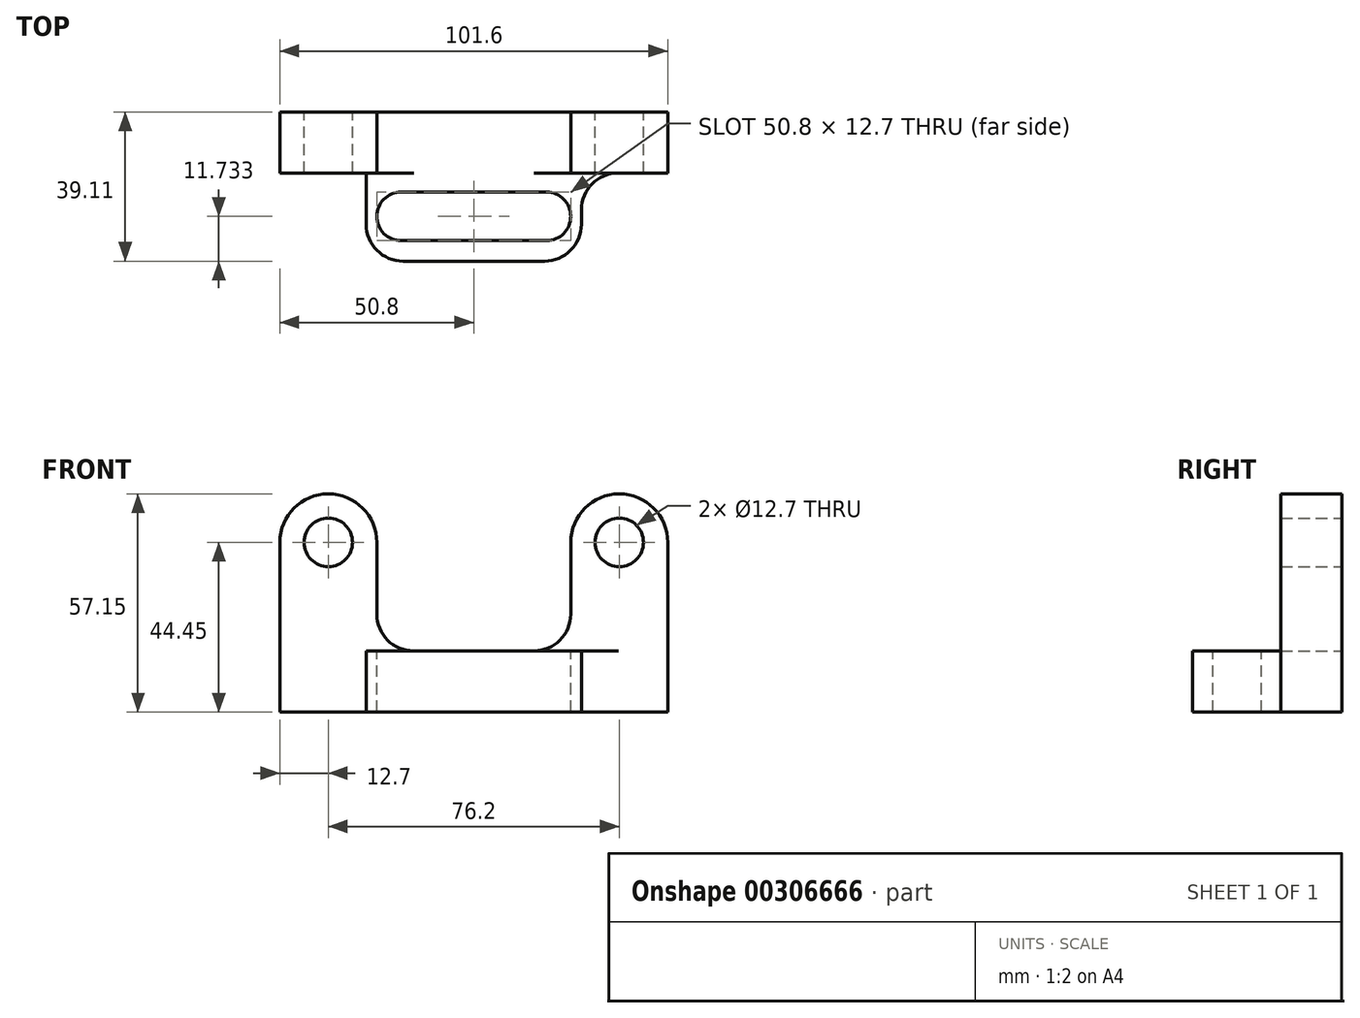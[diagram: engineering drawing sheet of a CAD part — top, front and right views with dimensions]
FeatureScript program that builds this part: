
annotation { "Feature Type Name" : "Feature", "Feature Type Description" : "" }
export const myFeature = defineFeature(function(context is Context, id is Id, definition is map)
    precondition{}
    {
        {
            var Q0;
            Q0=qCreatedBy(makeId("Front.planeOp"),FACE);
            var sketch = newSketch(context, id + "F0", { "sketchPlane" : qUnion([Q0])});
            skLineSegment(sketch, "E0", {"start": v(0, 0) * mm, "end": v(-50.8, 0) * mm});
            skLineSegment(sketch, "E1", {"start": v(-50.8, 0) * mm, "end": v(-50.8, 44.45) * mm});
            skLineSegment(sketch, "E2", {"start": v(-25.4, 44.45) * mm, "end": v(-25.4, 16) * mm});
            skLineSegment(sketch, "E3", {"start": v(-25.4, 16) * mm, "end": v(0, 16) * mm});
            skLineSegment(sketch, "E4", {"start": v(0, 0) * mm, "end": v(0, 78.5) * mm, "construction": true});
            skLineSegment(sketch, "E5.MirrorCS", {"start": v(25.4, 16) * mm, "end": v(0, 16) * mm});
            skLineSegment(sketch, "E6.MirrorCS", {"start": v(25.4, 44.45) * mm, "end": v(25.4, 16) * mm});
            skLineSegment(sketch, "E7.MirrorCS", {"start": v(50.8, 0) * mm, "end": v(50.8, 44.45) * mm});
            skLineSegment(sketch, "E8.MirrorCS", {"start": v(0, 0) * mm, "end": v(50.8, 0) * mm});
            skCircle(sketch, "E9", {"center": v(38.1, 44.45) * mm, "radius": 6.35 * mm});
            skCircle(sketch, "E10.MirrorC", {"center": v(-38.1, 44.45) * mm, "radius": 6.35 * mm});
            skLineSegment(sketch, "E11", {"start": v(38.1, 44.45) * mm, "end": v(38.1, 67.53) * mm, "construction": true});
            skLineSegment(sketch, "E12", {"start": v(-38.1, 44.45) * mm, "end": v(-38.1, 65.76) * mm, "construction": true});
            skArc(sketch, "E13", {"start": v(38.1, 57.15) * mm, "mid": v(29.12, 53.43) * mm, "end": v(25.4, 44.45) * mm});
            skArc(sketch, "E14", {"start": v(38.1, 57.15) * mm, "mid": v(47.08, 53.43) * mm, "end": v(50.8, 44.45) * mm});
            skArc(sketch, "E15.MirrorCS", {"start": v(-38.1, 57.15) * mm, "mid": v(-29.12, 53.43) * mm, "end": v(-25.4, 44.45) * mm});
            skArc(sketch, "E16.MirrorCS", {"start": v(-38.1, 57.15) * mm, "mid": v(-47.08, 53.43) * mm, "end": v(-50.8, 44.45) * mm});
            skPoint(sketch, "E17.orphan", {"position": v(50.8, 57.15) * mm});
            skPoint(sketch, "E18.MirrorCS.end.orphan", {"position": v(25.4, 57.15) * mm});
            skPoint(sketch, "E19.orphan", {"position": v(-25.4, 57.15) * mm});
            skPoint(sketch, "E20.orphan", {"position": v(-50.8, 57.15) * mm});
            skSolve(sketch);
        }
        {
            var Q0;
            {var subQ5=sQuery(id+"F0.wireOp",EDGE,"E0");Q0=makeQuery(id+"F0.imprint","IMPRINT",FACE,{"disambiguationData":[TD([[makeQuery(id+"F0.imprint","IMPRINT",EDGE,{"derivedFrom":subQ5}),-1.0]])]});}
            extrude(context, id + "F1", {"entities" : qUnion([Q0]), "depth" : 16 * mm});
        }
        {
            var Q0;
            Q0=makeQuery(id+"F0.imprint","IMPRINT",FACE,{"disambiguationData":[TD([[makeQuery(id+"F0.imprint","IMPRINT",EDGE,{"derivedFrom":sQuery(id+"F0.wireOp",EDGE,"E0")}),-1.0]])]});
            extrude(context, id + "F2", {"entities" : qUnion([Q0]), "operationType" : NewBodyOperationType.ADD, "depth" : 16 * mm});
        }
        {
            var Q0;
            Q0=makeQuery(id+"F1.opExtrude","SWEPT_EDGE",EDGE,{"disambiguationData":[OSD([sQuery(id+"F0.wireOp",EDGE,"E2"),sQuery(id+"F0.wireOp",EDGE,"E3")])]});
            var Q1;
            Q1=makeQuery(id+"F1.opExtrude","SWEPT_EDGE",EDGE,{"disambiguationData":[OSD([sQuery(id+"F0.wireOp",EDGE,"E5.MirrorCS"),sQuery(id+"F0.wireOp",EDGE,"E6.MirrorCS")])]});
            fillet(context, id + "F3", {"entities" : qUnion([Q0, Q1]), "radius" : 9.65 * mm, "tangentPropagation" : true, "allowEdgeOverflow" : false});
        }
        {
            var Q0;
            Q0=qCreatedBy(makeId("Top.planeOp"),FACE);
            var sketch = newSketch(context, id + "F4", { "sketchPlane" : qUnion([Q0])});
            skLineSegment(sketch, "E21", {"start": v(28.17, -16) * mm, "end": v(28.17, -39.11) * mm});
            skLineSegment(sketch, "E22.MirrorCS", {"start": v(-28.17, -16) * mm, "end": v(-28.17, -39.11) * mm});
            skLineSegment(sketch, "E23", {"start": v(-28.17, -39.11) * mm, "end": v(28.17, -39.11) * mm});
            skLineSegment(sketch, "E24", {"start": v(-28.17, -16) * mm, "end": v(28.17, -16) * mm});
            skSolve(sketch);
        }
        {
            var Q0;
            Q0=makeQuery(id+"F4.imprint","IMPRINT",FACE,{"disambiguationData":[TD([[makeQuery(id+"F4.imprint","IMPRINT",EDGE,{"derivedFrom":sQuery(id+"F4.wireOp",EDGE,"E21")}),-1.0]])]});
            extrude(context, id + "F5", {"entities" : qUnion([Q0]), "operationType" : NewBodyOperationType.ADD, "depth" : 16 * mm});
        }
        {
            var Q0;
            Q0=makeQuery(id+"F5.boolean.opBoolean","MERGE",FACE,{"derivedFrom":[makeQuery(id+"F1.opExtrude","SWEPT_FACE",FACE,{"disambiguationData":[OSD([sQuery(id+"F0.wireOp",EDGE,"E3"),sQuery(id+"F0.wireOp",EDGE,"E5.MirrorCS")])]}),makeQuery(id+"F5.opExtrude","CAP_FACE",FACE,{"disambiguationData":[OSD([sQuery(id+"F4.wireOp",EDGE,"E21"),sQuery(id+"F4.wireOp",EDGE,"KRn6xeVq-3zaL-ZNE9-6kKy-dGFoVnLs3Zqx"),sQuery(id+"F4.wireOp",EDGE,"ae659aa5-0c71-4b39-b7c4-d228686435f50.MirrorCS"),sQuery(id+"F4.wireOp",EDGE,"E22.MirrorCS"),sQuery(id+"F4.wireOp",EDGE,"PJdEW5La-l0Tz-svzj-1M6O-rA534kSb0CCf"),sQuery(id+"F4.wireOp",EDGE,"3d896502-7fe0-40ef-a271-82883b495ef90.MirrorCS")])],"isStart":false})]});
            var sketch = newSketch(context, id + "F6", { "sketchPlane" : qUnion([Q0])});
            skLineSegment(sketch, "E25", {"start": v(0, -21.03) * mm, "end": v(19.05, -21.03) * mm});
            skLineSegment(sketch, "E26", {"start": v(0, -33.73) * mm, "end": v(19.05, -33.73) * mm});
            skArc(sketch, "E27", {"start": v(19.05, -33.73) * mm, "mid": v(25.4, -27.38) * mm, "end": v(19.05, -21.03) * mm});
            skLineSegment(sketch, "E28.MirrorCS", {"start": v(0, -21.03) * mm, "end": v(-19.05, -21.03) * mm});
            skLineSegment(sketch, "E29.MirrorCS", {"start": v(0, -33.73) * mm, "end": v(-19.05, -33.73) * mm});
            skArc(sketch, "E30.MirrorCS", {"start": v(-19.05, -33.73) * mm, "mid": v(-25.4, -27.38) * mm, "end": v(-19.05, -21.03) * mm});
            skSolve(sketch);
        }
        {
            var Q0;
            Q0=makeQuery(id+"F5.opExtrude","SWEPT_EDGE",EDGE,{"disambiguationData":[OSD([sQuery(id+"F4.wireOp",EDGE,"E21"),sQuery(id+"F4.wireOp",EDGE,"E23")])]});
            var Q1;
            Q1=makeQuery(id+"F5.opExtrude","SWEPT_EDGE",EDGE,{"disambiguationData":[OSD([sQuery(id+"F4.wireOp",EDGE,"E22.MirrorCS"),sQuery(id+"F4.wireOp",EDGE,"E23")])]});
            var Q2;
            Q2=makeQuery(id+"F5.opExtrude","SWEPT_EDGE",EDGE,{"disambiguationData":[OSD([sQuery(id+"F4.wireOp",EDGE,"E21"),sQuery(id+"F4.wireOp",EDGE,"E24")])]});
            var Q3;
            Q3=makeQuery(id+"F5.opExtrude","SWEPT_EDGE",EDGE,{"disambiguationData":[OSD([sQuery(id+"F4.wireOp",EDGE,"E22.MirrorCS"),sQuery(id+"F4.wireOp",EDGE,"E24")])]});
            fillet(context, id + "F7", {"entities" : qUnion([Q0, Q1, Q2, Q3]), "radius" : 9.65 * mm, "tangentPropagation" : true, "allowEdgeOverflow" : false});
        }
        {
            var Q0;
            Q0=makeQuery(id+"F6.imprint","IMPRINT",FACE,{"disambiguationData":[TD([[makeQuery(id+"F6.imprint","IMPRINT",EDGE,{"derivedFrom":sQuery(id+"F6.wireOp",EDGE,"E25")}),-1.0]])]});
            extrude(context, id + "F8", {"entities" : qUnion([Q0]), "operationType" : NewBodyOperationType.REMOVE, "endBound" : BoundingType.THROUGH_ALL, "oppositeDirection" : true, "depth" : 25.4 * mm});
        }
    });
